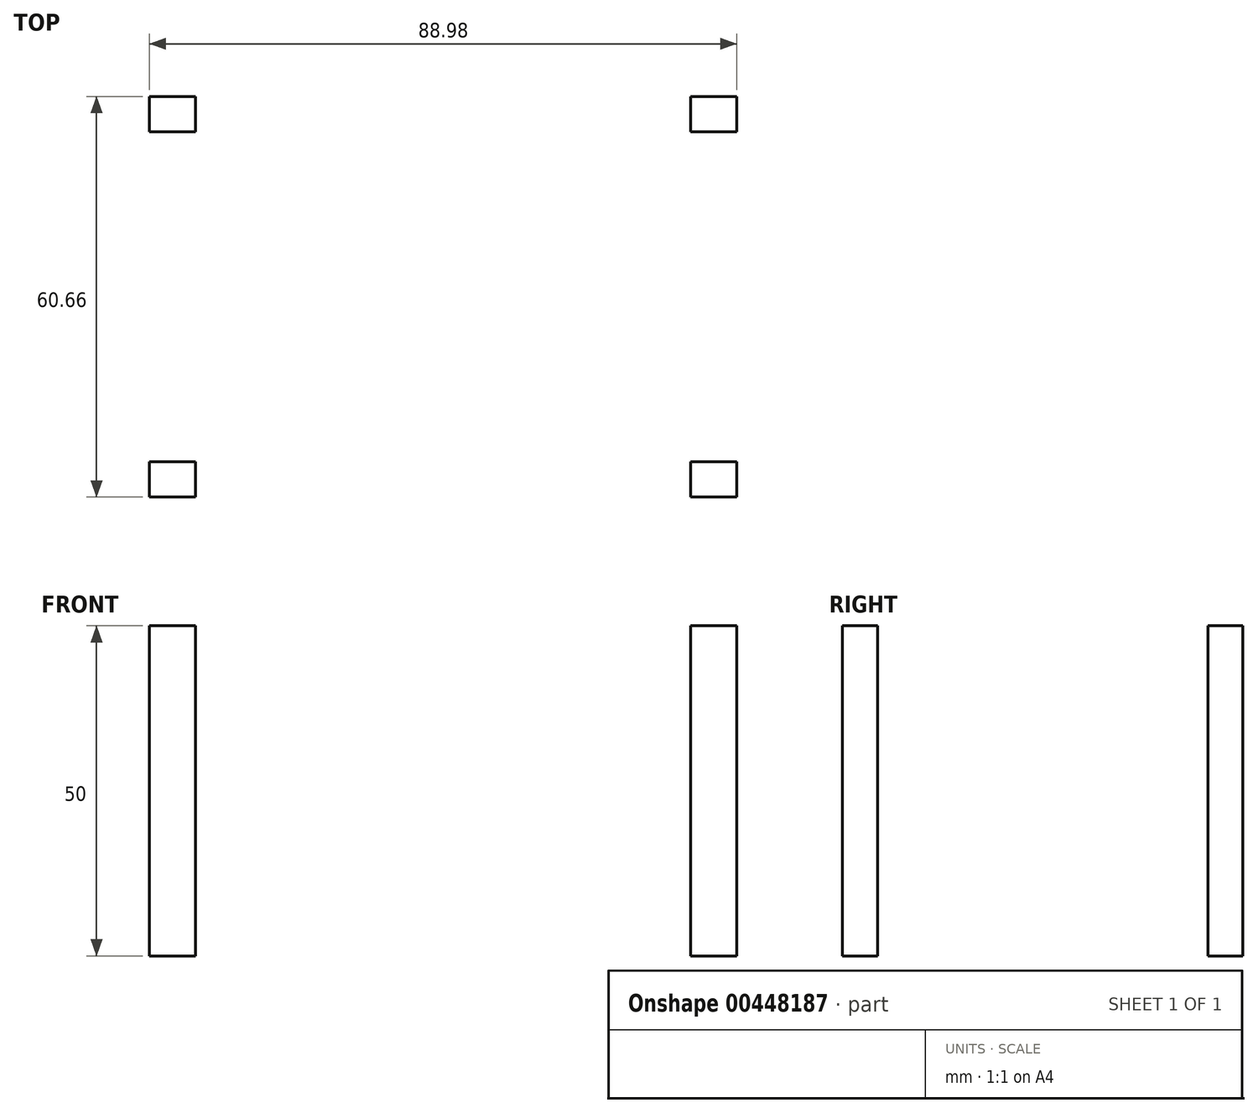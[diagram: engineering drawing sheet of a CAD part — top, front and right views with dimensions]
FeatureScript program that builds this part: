
annotation { "Feature Type Name" : "Feature", "Feature Type Description" : "" }
export const myFeature = defineFeature(function(context is Context, id is Id, definition is map)
    precondition{}
    {
        {
            var Q0;
            Q0=qCreatedBy(makeId("Top.planeOp"),FACE);
            var sketch = newSketch(context, id + "F0", { "sketchPlane" : qUnion([Q0])});
            skLineSegment(sketch, "E0.bottom", {"start": v(-44.49, 30.33) * mm, "end": v(-37.5, 30.33) * mm});
            skLineSegment(sketch, "E0.top", {"start": v(-44.49, 25) * mm, "end": v(-37.5, 25) * mm});
            skLineSegment(sketch, "E0.left", {"start": v(-44.49, 30.33) * mm, "end": v(-44.49, 25) * mm});
            skLineSegment(sketch, "E0.right", {"start": v(-37.5, 30.33) * mm, "end": v(-37.5, 25) * mm});
            skLineSegment(sketch, "E1.MirrorCS", {"start": v(44.49, 30.33) * mm, "end": v(37.5, 30.33) * mm});
            skLineSegment(sketch, "E2.MirrorCS", {"start": v(44.49, 25) * mm, "end": v(37.5, 25) * mm});
            skLineSegment(sketch, "E3.MirrorCS", {"start": v(44.49, 30.33) * mm, "end": v(44.49, 25) * mm});
            skLineSegment(sketch, "E4.MirrorCS", {"start": v(37.5, 30.33) * mm, "end": v(37.5, 25) * mm});
            skLineSegment(sketch, "E5.MirrorCS", {"start": v(44.49, -30.33) * mm, "end": v(37.5, -30.33) * mm});
            skLineSegment(sketch, "E6.MirrorCS", {"start": v(37.5, -30.33) * mm, "end": v(37.5, -25) * mm});
            skLineSegment(sketch, "E7.MirrorCS", {"start": v(44.49, -25) * mm, "end": v(37.5, -25) * mm});
            skLineSegment(sketch, "E8.MirrorCS", {"start": v(44.49, -30.33) * mm, "end": v(44.49, -25) * mm});
            skLineSegment(sketch, "E9.MirrorCS", {"start": v(-44.49, -30.33) * mm, "end": v(-37.5, -30.33) * mm});
            skLineSegment(sketch, "E10.MirrorCS", {"start": v(-44.49, -30.33) * mm, "end": v(-44.49, -25) * mm});
            skLineSegment(sketch, "E11.MirrorCS", {"start": v(-44.49, -25) * mm, "end": v(-37.5, -25) * mm});
            skLineSegment(sketch, "E12.MirrorCS", {"start": v(-37.5, -30.33) * mm, "end": v(-37.5, -25) * mm});
            skSolve(sketch);
        }
        {
            var Q0;
            Q0 = qSketchRegion(id + "F0", true);
            extrude(context, id + "F1", {"entities" : qUnion([Q0]), "depth" : 50 * mm});
        }
    });
